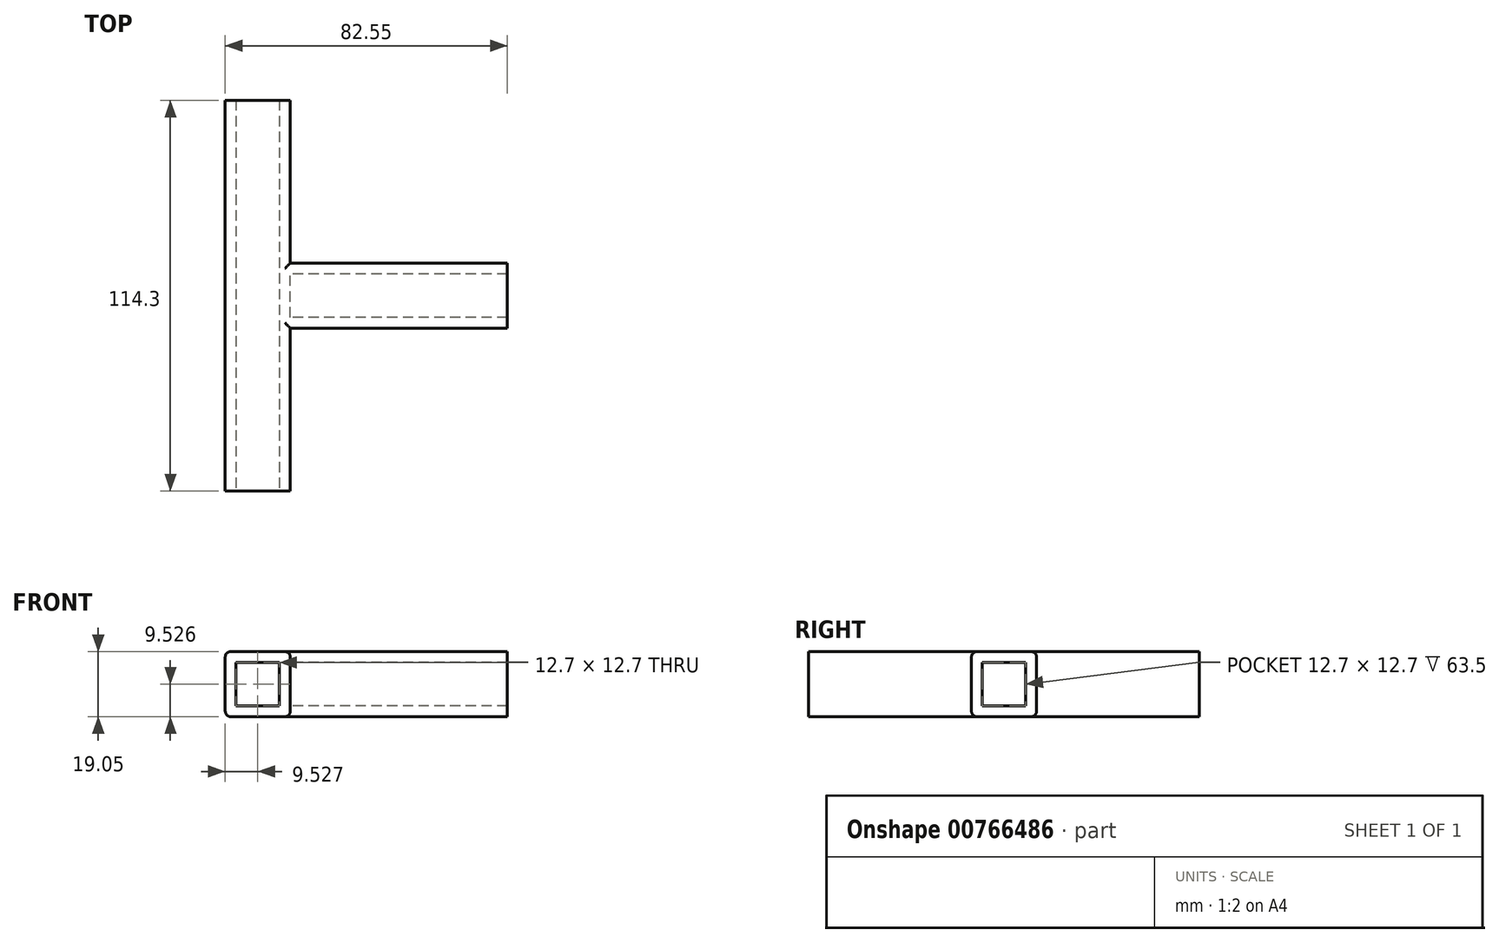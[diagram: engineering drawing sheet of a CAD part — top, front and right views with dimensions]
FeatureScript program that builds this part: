
annotation { "Feature Type Name" : "Feature", "Feature Type Description" : "" }
export const myFeature = defineFeature(function(context is Context, id is Id, definition is map)
    precondition{}
    {
        {
            var Q0;
            Q0=qCreatedBy(makeId("Front.planeOp"),FACE);
            var sketch = newSketch(context, id + "F0", { "sketchPlane" : qUnion([Q0])});
            skLineSegment(sketch, "E0.bottom", {"start": v(-90.1, 128.77) * mm, "end": v(-71.06, 128.77) * mm});
            skLineSegment(sketch, "E0.top", {"start": v(-90.1, 109.72) * mm, "end": v(-71.06, 109.72) * mm});
            skLineSegment(sketch, "E0.left", {"start": v(-90.1, 128.77) * mm, "end": v(-90.1, 109.72) * mm});
            skLineSegment(sketch, "E0.right", {"start": v(-71.06, 128.77) * mm, "end": v(-71.06, 109.72) * mm});
            skLineSegment(sketch, "E1.0", {"start": v(-86.93, 125.6) * mm, "end": v(-74.23, 125.6) * mm});
            skLineSegment(sketch, "E1.1", {"start": v(-86.93, 125.6) * mm, "end": v(-86.93, 112.9) * mm});
            skLineSegment(sketch, "E1.2", {"start": v(-86.93, 112.9) * mm, "end": v(-74.23, 112.9) * mm});
            skLineSegment(sketch, "E1.3", {"start": v(-74.23, 125.6) * mm, "end": v(-74.23, 112.9) * mm});
            skSolve(sketch);
        }
        {
            var Q0;
            Q0=qSketchRegion(id+"F0",true);
            extrude(context, id + "F1", {"entities" : qUnion([Q0]), "oppositeDirection" : true, "depth" : 114.3 * mm, "offsetDistance" : 25.4 * mm});
        }
        {
            var Q0;
            Q0=makeQuery(id+"F1.opExtrude","SWEPT_FACE",FACE,{"disambiguationData":[OSD([sQuery(id+"F0.wireOp",EDGE,"E0.right")])]});
            var sketch = newSketch(context, id + "F2", { "sketchPlane" : qUnion([Q0])});
            skLineSegment(sketch, "E2.bottom", {"start": v(47.62, 109.72) * mm, "end": v(66.67, 109.72) * mm});
            skLineSegment(sketch, "E2.top", {"start": v(47.62, 128.77) * mm, "end": v(66.67, 128.77) * mm});
            skLineSegment(sketch, "E2.left", {"start": v(47.62, 109.72) * mm, "end": v(47.62, 128.77) * mm});
            skLineSegment(sketch, "E2.right", {"start": v(66.67, 109.72) * mm, "end": v(66.67, 128.77) * mm});
            skLineSegment(sketch, "E3.0", {"start": v(50.8, 125.6) * mm, "end": v(63.5, 125.6) * mm});
            skLineSegment(sketch, "E3.1", {"start": v(50.8, 112.9) * mm, "end": v(50.8, 125.6) * mm});
            skLineSegment(sketch, "E3.2", {"start": v(50.8, 112.9) * mm, "end": v(63.5, 112.9) * mm});
            skLineSegment(sketch, "E3.3", {"start": v(63.5, 112.9) * mm, "end": v(63.5, 125.6) * mm});
            skSolve(sketch);
        }
        {
            var Q0;
            Q0=qSketchRegion(id+"F2",true);
            extrude(context, id + "F3", {"entities" : qUnion([Q0]), "operationType" : NewBodyOperationType.ADD, "depth" : 63.5 * mm, "offsetDistance" : 25.4 * mm});
        }
        {
            var Q0;
            {var subQ0=sQuery(id+"F0.wireOp",EDGE,"E0.right");var subQ1=sQuery(id+"F0.wireOp",EDGE,"E0.bottom");Q0=makeQuery(id+"F3.boolean.opBoolean","SPLIT",EDGE,{"disambiguationData":[TD([makeQuery(id+"F3.opExtrude","SWEPT_FACE",FACE,{"disambiguationData":[OSD([sQuery(id+"F2.wireOp",EDGE,"E2.left")])]})])],"derivedFrom":makeQuery(id+"F1.opExtrude","SWEPT_EDGE",EDGE,{"disambiguationData":[OSD([subQ1,subQ0])]})});}
            var Q1;
            Q1=makeQuery(id+"F3.opExtrude","SWEPT_EDGE",EDGE,{"disambiguationData":[OSD([sQuery(id+"F0.wireOp",EDGE,"E0.bottom"),sQuery(id+"F0.wireOp",EDGE,"E0.right"),sQuery(id+"F2.wireOp",EDGE,"E2.top"),sQuery(id+"F2.wireOp",EDGE,"E2.left")])]});
            var Q2;
            Q2=makeQuery(id+"F1.opExtrude","SWEPT_EDGE",EDGE,{"disambiguationData":[OSD([sQuery(id+"F0.wireOp",EDGE,"E0.bottom"),sQuery(id+"F0.wireOp",EDGE,"E0.left")])]});
            var Q3;
            {var subQ0=sQuery(id+"F0.wireOp",EDGE,"E0.right");var subQ1=sQuery(id+"F0.wireOp",EDGE,"E0.top");Q3=makeQuery(id+"F3.boolean.opBoolean","SPLIT",EDGE,{"disambiguationData":[TD([makeQuery(id+"F3.opExtrude","SWEPT_FACE",FACE,{"disambiguationData":[OSD([sQuery(id+"F2.wireOp",EDGE,"E2.left")])]})])],"derivedFrom":makeQuery(id+"F1.opExtrude","SWEPT_EDGE",EDGE,{"disambiguationData":[OSD([subQ1,subQ0])]})});}
            var Q4;
            Q4=makeQuery(id+"F3.opExtrude","SWEPT_EDGE",EDGE,{"disambiguationData":[OSD([sQuery(id+"F0.wireOp",EDGE,"E0.top"),sQuery(id+"F0.wireOp",EDGE,"E0.right"),sQuery(id+"F2.wireOp",EDGE,"E2.bottom"),sQuery(id+"F2.wireOp",EDGE,"E2.left")])]});
            var Q5;
            {var subQ0=sQuery(id+"F0.wireOp",EDGE,"E0.right");var subQ1=sQuery(id+"F0.wireOp",EDGE,"E0.bottom");Q5=makeQuery(id+"F3.boolean.opBoolean","SPLIT",EDGE,{"disambiguationData":[TD([makeQuery(id+"F3.opExtrude","SWEPT_FACE",FACE,{"disambiguationData":[OSD([sQuery(id+"F2.wireOp",EDGE,"E2.right")])]})])],"derivedFrom":makeQuery(id+"F1.opExtrude","SWEPT_EDGE",EDGE,{"disambiguationData":[OSD([subQ1,subQ0])]})});}
            var Q6;
            {var subQ0=sQuery(id+"F0.wireOp",EDGE,"E0.right");var subQ1=sQuery(id+"F0.wireOp",EDGE,"E0.top");Q6=makeQuery(id+"F3.boolean.opBoolean","SPLIT",EDGE,{"disambiguationData":[TD([makeQuery(id+"F3.opExtrude","SWEPT_FACE",FACE,{"disambiguationData":[OSD([sQuery(id+"F2.wireOp",EDGE,"E2.right")])]})])],"derivedFrom":makeQuery(id+"F1.opExtrude","SWEPT_EDGE",EDGE,{"disambiguationData":[OSD([subQ1,subQ0])]})});}
            var Q7;
            Q7=makeQuery(id+"F3.opExtrude","SWEPT_EDGE",EDGE,{"disambiguationData":[OSD([sQuery(id+"F0.wireOp",EDGE,"E0.top"),sQuery(id+"F0.wireOp",EDGE,"E0.right"),sQuery(id+"F2.wireOp",EDGE,"E2.bottom"),sQuery(id+"F2.wireOp",EDGE,"E2.right")])]});
            var Q8;
            Q8=makeQuery(id+"F3.opExtrude","SWEPT_EDGE",EDGE,{"disambiguationData":[OSD([sQuery(id+"F0.wireOp",EDGE,"E0.bottom"),sQuery(id+"F0.wireOp",EDGE,"E0.right"),sQuery(id+"F2.wireOp",EDGE,"E2.top"),sQuery(id+"F2.wireOp",EDGE,"E2.right")])]});
            var Q9;
            Q9=makeQuery(id+"F1.opExtrude","SWEPT_EDGE",EDGE,{"disambiguationData":[OSD([sQuery(id+"F0.wireOp",EDGE,"E0.top"),sQuery(id+"F0.wireOp",EDGE,"E0.left")])]});
            fillet(context, id + "F4", {"entities" : qUnion([Q0, Q1, Q2, Q3, Q4, Q5, Q6, Q7, Q8, Q9]), "radius" : 1.59 * mm, "tangentPropagation" : true, "allowEdgeOverflow" : false});
        }
    });
